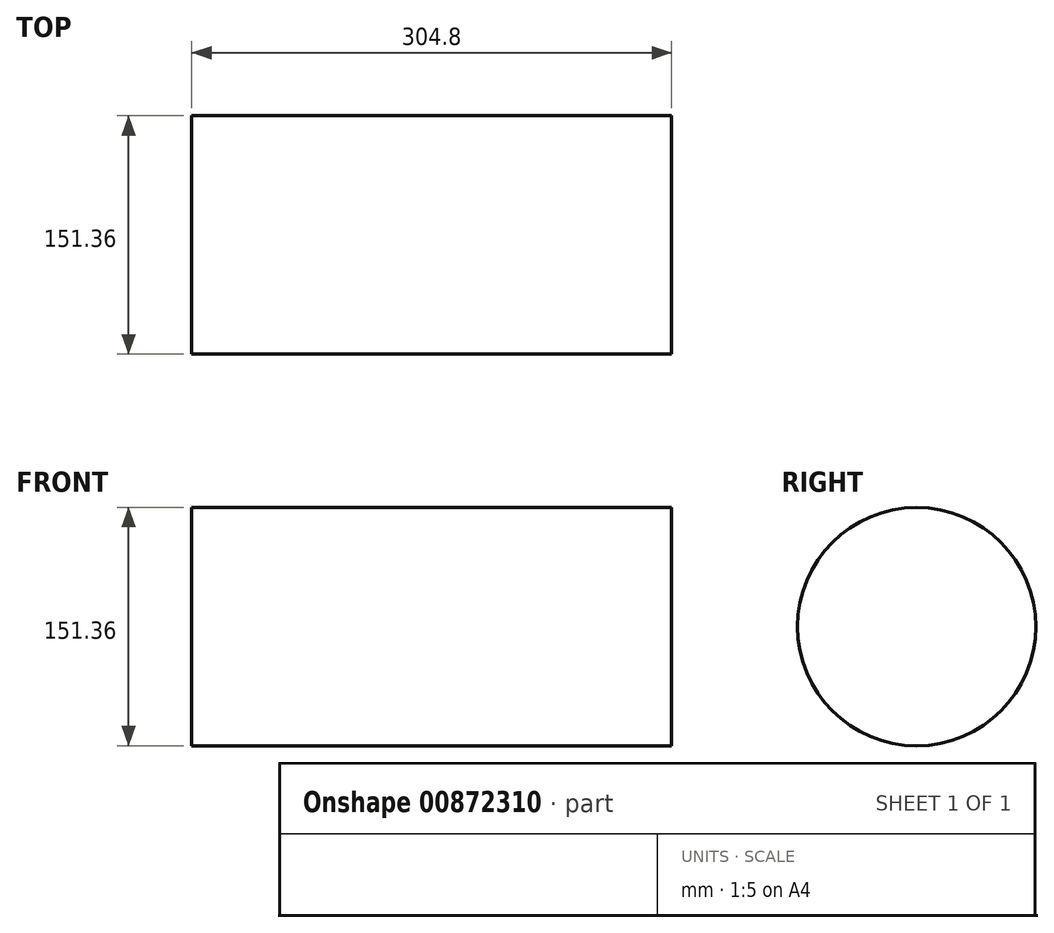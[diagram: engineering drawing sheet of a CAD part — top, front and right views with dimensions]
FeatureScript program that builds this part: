
annotation { "Feature Type Name" : "Feature", "Feature Type Description" : "" }
export const myFeature = defineFeature(function(context is Context, id is Id, definition is map)
    precondition{}
    {
        {
            var Q0;
            Q0=qCreatedBy(makeId("Right.planeOp"),FACE);
            var sketch = newSketch(context, id + "F0", { "sketchPlane" : qUnion([Q0])});
            skCircle(sketch, "E0", {"center": v(0, 0) * mm, "radius": 75.68 * mm});
            skSolve(sketch);
        }
        {
            var Q0;
            Q0 = qSketchRegion(id + "F0", true);
            extrude(context, id + "F1", {"entities" : qUnion([Q0]), "endBound" : BoundingType.SYMMETRIC, "depth" : 304.8 * mm, "offsetDistance" : 25.4 * mm});
        }
    });
